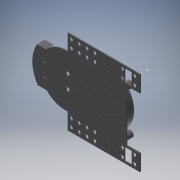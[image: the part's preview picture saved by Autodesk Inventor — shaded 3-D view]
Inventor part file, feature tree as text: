
AUTODESK INVENTOR PART (.ipt)
format: ipt  version: 2016 (Build 200138000, 138)  size: 288,256 bytes
history: native  units: mm
features: sketch x9, extrude x4, hole x4
ambient origin geometry x8: Origin, YZ Plane, XZ Plane, XY Plane, X Axis, Y Axis, Z Axis, Center Point
bodies: Solid1 (feature_tree)
feature tree (17):
  extrude  "Extrusion1"  Depth=106.0mm
  hole  "Hole1"  [1 undecoded]
  extrude  "Extrusion2"  Depth=24.0mm
  hole  "Hole2"  [1 undecoded]
  hole  "Hole3"  [1 undecoded]
  extrude  "Extrusion3"  Depth=5.0mm
  hole  "Hole5"  [1 undecoded]
  extrude  "Extrusion6"  Depth=5.0mm
  sketch  "Sketch17"  dims[d19=5.0mm d20=5.0mm d21=6.0mm d22=4.0mm d23=2.0mm d24=90.0deg d25=8.0mm d26=20.594885mm d27=11.0mm d28=18.0mm d29=3.25mm d30=3.0mm d31=6.0mm d32=1.5mm d33=0.0mm d34=5.0mm d35=5.0mm d36=6.0mm d37=5.0mm d38=11.5mm d39=5.0mm d40=11.5mm d41=5.0mm d42=5.75mm d43=5.0mm d44=6.0mm d45=4.0mm d46=2.0mm d47=90.0deg d48=8.0mm d49=20.594885mm d56=10.0mm d57=10.0mm d58=34.0mm d60=5.5mm d61=5.5mm d62=5.5mm d63=5.5mm d64=5.5mm d65=6.0mm d66=4.0mm d67=2.0mm d68=90.0deg d69=8.0mm d70=20.594885mm d71=8.0mm d72=13.0mm d80=10.0mm d82=25.0mm d85=8.0mm d86=10.0mm d87=0.0mm d103=10.0mm d104=13.0mm d112=6.0mm d113=6.0mm d114=6.0mm d115=6.0mm d116=6.0mm d117=4.0mm d118=2.0mm d119=90.0deg d120=10.0mm d121=0.0mm d122=1.5mm d123=0.0mm d125=63.0mm d126=6.5mm d127=6.5mm d128=137.741536mm d129=36.0mm d91=1.0mm d92=1.0mm]
  sketch  "Sketch1"  dims[d0=24.0mm d2=106.0mm]
  sketch  "Sketch2"  dims[d3=24.0mm d4=20.0mm]
  sketch  "Sketch3"  dims[d5=76.0mm d6=24.0mm]
  sketch  "Sketch4"  dims[d7=106.0mm d8=24.0mm]
  sketch  "Sketch5"  dims[d9=1.5mm d10=0.0mm]
  sketch  "Sketch6"  dims[d11=5.0mm d12=8.0mm]
  sketch  "Sketch14"  dims[d15=18.0mm d16=12.0mm]
  sketch  "Sketch16"  dims[d17=5.0mm d18=5.0mm]
note: 4 required parameter values undecoded (feature->parameter linkage not recoverable at this tier; creation-order binding heuristic only, values carry confidence <= 0.55)
